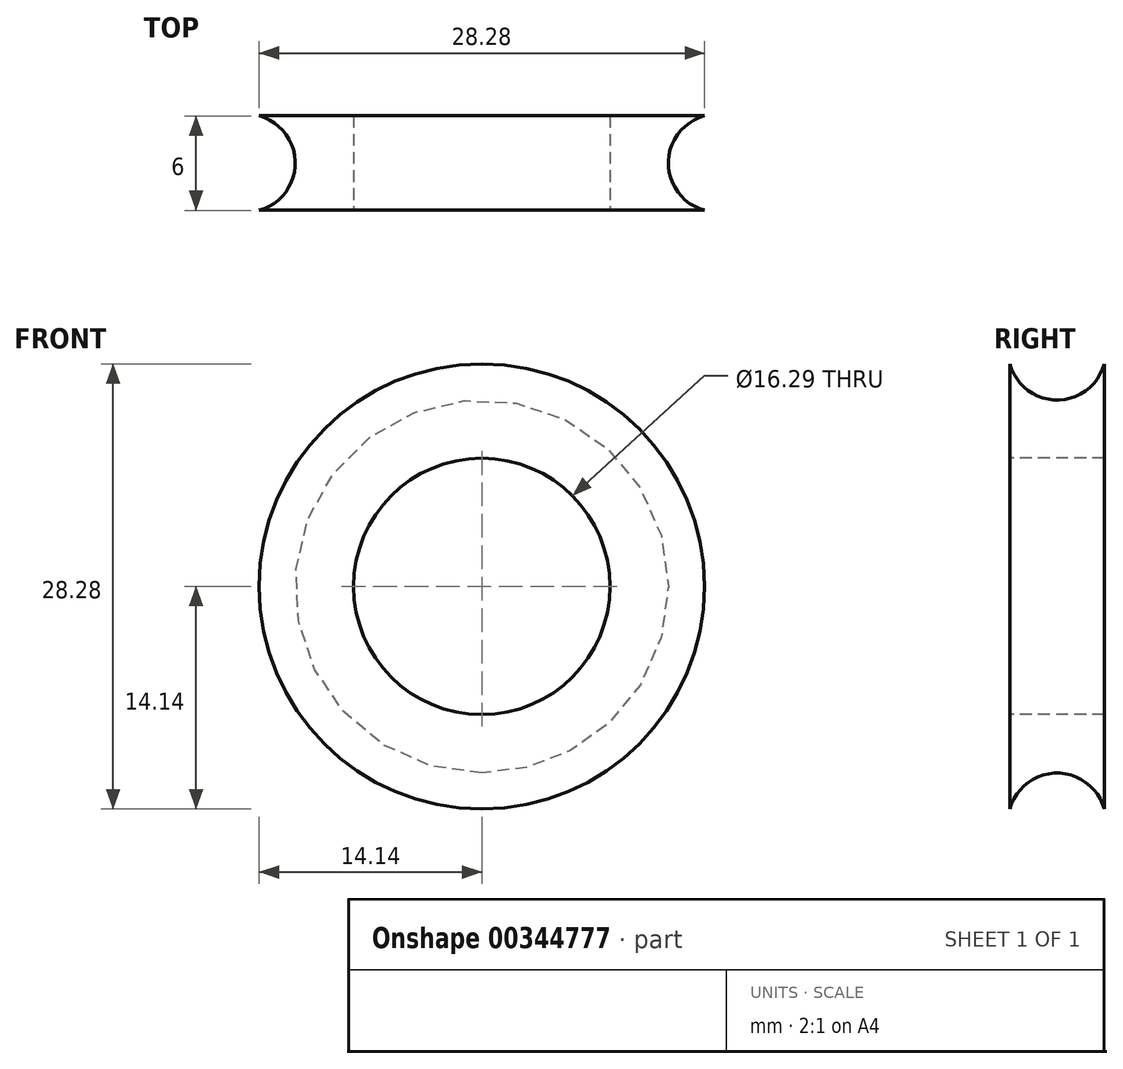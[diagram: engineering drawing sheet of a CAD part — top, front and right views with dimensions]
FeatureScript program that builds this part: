
annotation { "Feature Type Name" : "Feature", "Feature Type Description" : "" }
export const myFeature = defineFeature(function(context is Context, id is Id, definition is map)
    precondition{}
    {
        {
            var Q0;
            Q0=qCreatedBy(makeId("Top.planeOp"),FACE);
            var sketch = newSketch(context, id + "F0", { "sketchPlane" : qUnion([Q0])});
            skLineSegment(sketch, "E0.bottom", {"start": v(8.14, 40.8) * mm, "end": v(14.14, 40.8) * mm});
            skLineSegment(sketch, "E0.top", {"start": v(8.14, 34.8) * mm, "end": v(14.14, 34.8) * mm});
            skLineSegment(sketch, "E0.left", {"start": v(8.14, 40.8) * mm, "end": v(8.14, 34.8) * mm});
            skArc(sketch, "E1", {"start": v(14.14, 40.8) * mm, "mid": v(11.85, 37.8) * mm, "end": v(14.14, 34.8) * mm});
            skLineSegment(sketch, "E2", {"start": v(0, 23.36) * mm, "end": v(0, 46.03) * mm});
            skSolve(sketch);
        }
        {
            var Q0;
            Q0=makeQuery(id+"F0.imprint","IMPRINT",FACE,{"disambiguationData":[TD([[makeQuery(id+"F0.imprint","IMPRINT",EDGE,{"derivedFrom":sQuery(id+"F0.wireOp",EDGE,"E0.bottom")}),-1.0]])]});
            var Q1;
            Q1=sQuery(id+"F0.wireOp",EDGE,"E2");
            revolve(context, id + "F1", {"entities" : qUnion([Q0]), "axis" : qUnion([Q1]), "revolveType" : RevolveType.FULL});
        }
    });
